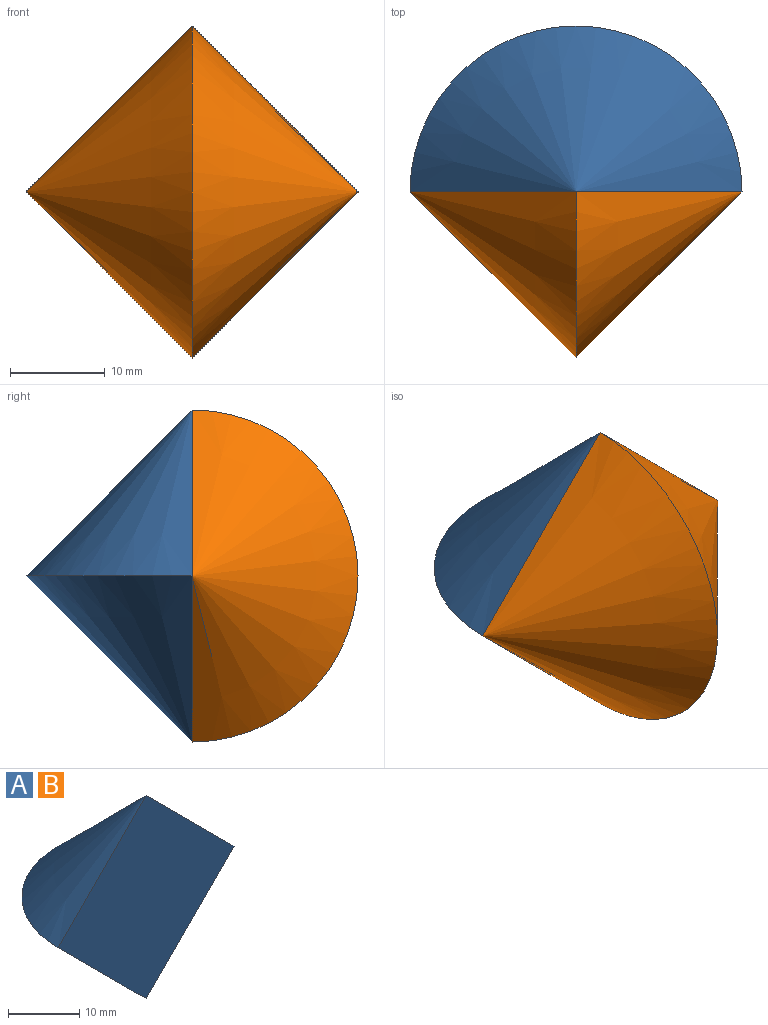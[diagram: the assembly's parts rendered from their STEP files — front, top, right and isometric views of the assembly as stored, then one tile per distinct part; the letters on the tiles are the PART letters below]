
ASSEMBLY  parts=2 mates=1
PART A: 3 faces, bbox 35x17.5x35 mm
  f0: cone r=17.5mm half-angle=45deg, axis (0,0,-1), area 680.3mm2, adj f1,f2
  f1: cone r=0mm half-angle=45deg, axis (0,0,1), area 680.3mm2, adj f0,f2
  f2: plane 35x35mm, normal (0,-1,0), area 612.5mm2, adj f0,f1
PART B: same geometry as A
PLACE A at identity
PLACE B rot(axis=(0.71,0,0.71),180deg) t=(0,0,0)mm
MATE fastened B.f2 <-> A.f2  axis (0,1,0) through (0,0,0)mm
